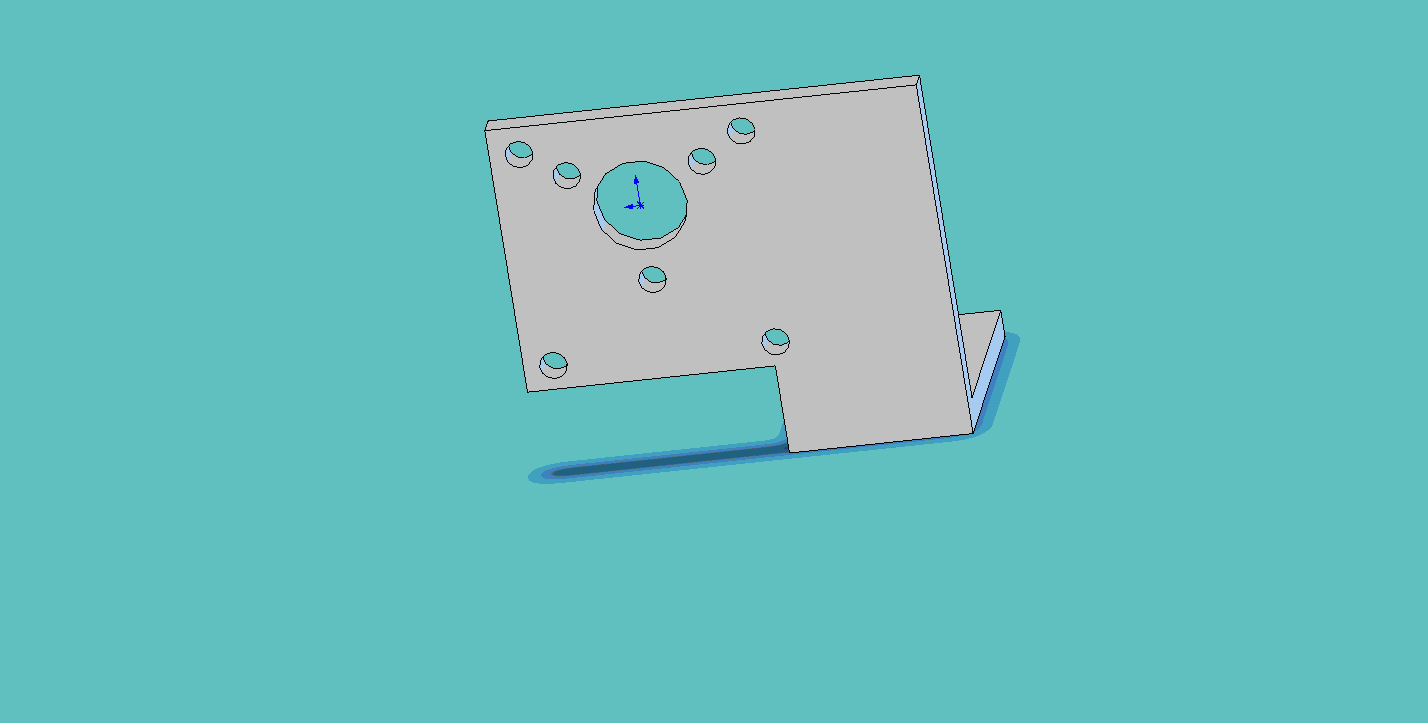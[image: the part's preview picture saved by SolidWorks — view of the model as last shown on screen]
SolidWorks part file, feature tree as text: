
SOLIDWORKS PART (.sldprt)
format: sldprt  version: not decoded by parser v0  size: 232,960 bytes
history: native  units: mm
features: plane x3, sketch x3, extrude x2, material x1, cut_extrude x1 (+10 scaffold rows collapsed)
feature tree (20):
  scaffold x10  (default folders/planes/origin — collapsed)
  material  "Matériau <non spécifié>"
  plane  "Plan de face"
  plane  "Plan de dessus"
  plane  "Plan de droite"
  sketch  "Esquisse1"  dims[c1.D2=3.0mm c1.D9=~43.032661mm c1.D10=10.2mm c1.D13=3.0mm c1.D14=17.0mm c2.D9=10.2mm c2.D1=47.0mm c2.D3=24.2mm c2.D4=24.2mm c2.D5=3.1mm c2.D6=40.0mm c2.D7=20.0mm c2.D8=31.8mm c3.D9=29.6mm c3.D11=19.55mm c3.D12=10.0mm c3.D15=8.5mm c4.D15=120.0deg c4.D16=~7.630189mm c5.D16=120.0deg c5.D8=12.1mm c5.D9=7.2mm]
  extrude  "Extrusion1"  Depth=3mm
  sketch  "Esquisse2"  dims[D1=3.0mm]
  extrude  "Extrusion2"  Depth=27mm
  sketch  "Esquisse4"  dims[D1=4.2mm D2=8.0mm D3=12.0mm]
  cut_extrude  "Enlèv. mat.-Extru.1"  [1 undecoded]
decode coverage: 5 of 6 modeling features carry decoded parameters
note: ~ marks probable driven/reference dimensions
note: 1 parameter value undecoded
note: suppression state not decoded; provenance and decode notes live in map.json
